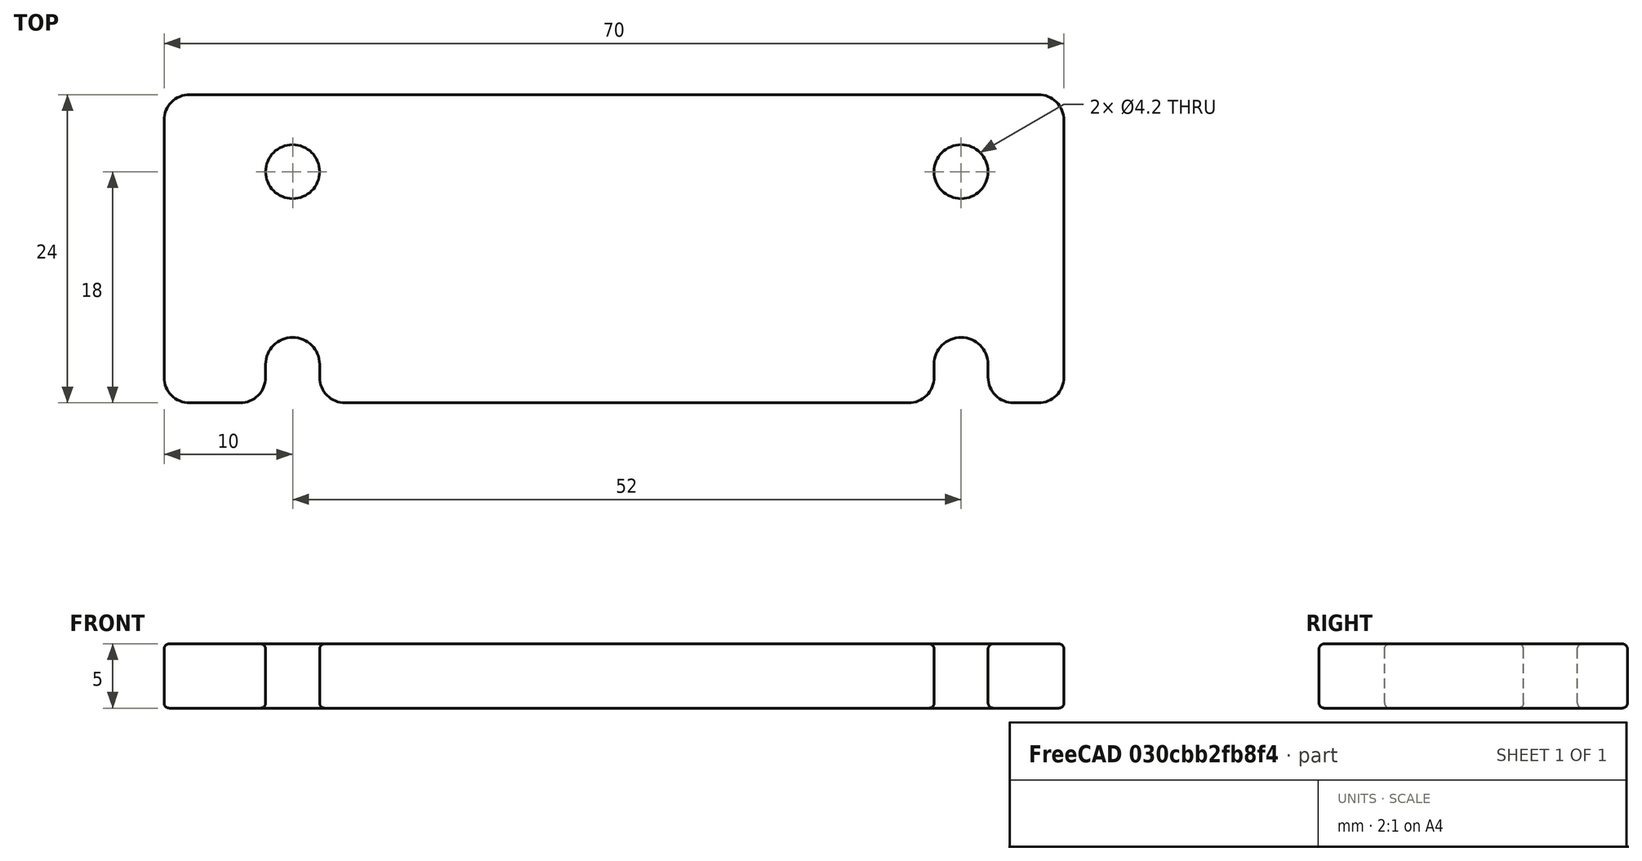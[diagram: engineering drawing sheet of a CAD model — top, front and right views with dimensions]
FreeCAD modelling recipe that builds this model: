
FCSTD DOCUMENT  (FreeCAD 0.20R24992 (Git))
Label: YACoverStepper_V1
License: All rights reserved
LicenseURL: http://en.wikipedia.org/wiki/All_rights_reserved
objects: Part::Cut×6, Part::Cylinder×4, Part::Box×3, Part::Fillet×2
note: 15 computed .brp shape members not serialized (recipe doc carries the construction recipe); baked Part::Feature solids carry a one-line shape summary decoded from their .brp

FEATURE [Part::Box] Box  label="Würfel"
  AttacherType = Attacher::AttachEngine3D
  Height = 5
  Length = 70
  Placement = pos=(-36,0,0) rot=(0,0,1;0rad)
  Width = 24
FEATURE [Part::Cylinder] Cylinder  label="Zylinder"
  Angle = 360
  AttacherType = Attacher::AttachEngine3D
  FirstAngle = 0
  Height = 10
  Placement = pos=(26,3,0) rot=(0,0,1;0rad)
  Radius = 2.1
  SecondAngle = 0
FEATURE [Part::Cylinder] Cylinder001  label="Zylinder001"
  Angle = 360
  AttacherType = Attacher::AttachEngine3D
  FirstAngle = 0
  Height = 10
  Placement = pos=(-26,3,0) rot=(0,0,1;0rad)
  Radius = 2.1
  SecondAngle = 0
FEATURE [Part::Cylinder] Cylinder002  label="Zylinder002"
  Angle = 360
  AttacherType = Attacher::AttachEngine3D
  FirstAngle = 0
  Height = 10
  Placement = pos=(-26,18,0) rot=(0,0,1;0rad)
  Radius = 2.1
  SecondAngle = 0
FEATURE [Part::Cylinder] Cylinder003  label="Zylinder003"
  Angle = 360
  AttacherType = Attacher::AttachEngine3D
  FirstAngle = 0
  Height = 10
  Placement = pos=(26,18,0) rot=(0,0,1;0rad)
  Radius = 2.1
  SecondAngle = 0
FEATURE [Part::Box] Box001  label="Würfel001"
  AttacherType = Attacher::AttachEngine3D
  Height = 10
  Length = 4.2
  Placement = pos=(23.9,0,0) rot=(0,0,1;0rad)
  Width = 3
FEATURE [Part::Box] Box002  label="Würfel002"
  AttacherType = Attacher::AttachEngine3D
  Height = 10
  Length = 4.2
  Placement = pos=(-28.1,0,0) rot=(0,0,1;0rad)
  Width = 3
FEATURE [Part::Cut] Cut
  Base = -> Box
  Tool = -> Cylinder
FEATURE [Part::Cut] Cut001
  Base = -> Cut
  Tool = -> Box002
FEATURE [Part::Cut] Cut002
  Base = -> Cut001
  Tool = -> Box001
FEATURE [Part::Cut] Cut003
  Base = -> Cut002
  Tool = -> Cylinder003
FEATURE [Part::Cut] Cut004
  Base = -> Cut003
  Tool = -> Cylinder002
FEATURE [Part::Cut] Cut005
  Base = -> Cut004
  Tool = -> Cylinder001
FEATURE [Part::Fillet] Fillet
  Base = -> Cut005
  Edges = 8 edges r=2: [Edge1,Edge3,Edge6,Edge21,Edge34,Edge35,Edge38,Edge39]
FEATURE [Part::Fillet] Fillet001
  Base = -> Fillet
  Edges = 43 edges r=0.4: [Edge1,Edge3,Edge5,Edge6,Edge7,Edge8,Edge9,Edge10,Edge11,Edge12,Edge13,Edge14,Edge15,Edge16,Edge17,Edge18,Edge19,Edge20,Edge21,Edge22,Edge23,Edge24,Edge25,Edge26,Edge28,Edge30,Edge31,Edge32,Edge33,Edge34,Edge35,Edge36,Edge37,Edge38,Edge39,Edge40,Edge41,Edge42,Edge44,Edge45,Edge46,Edge47,Edge48]
